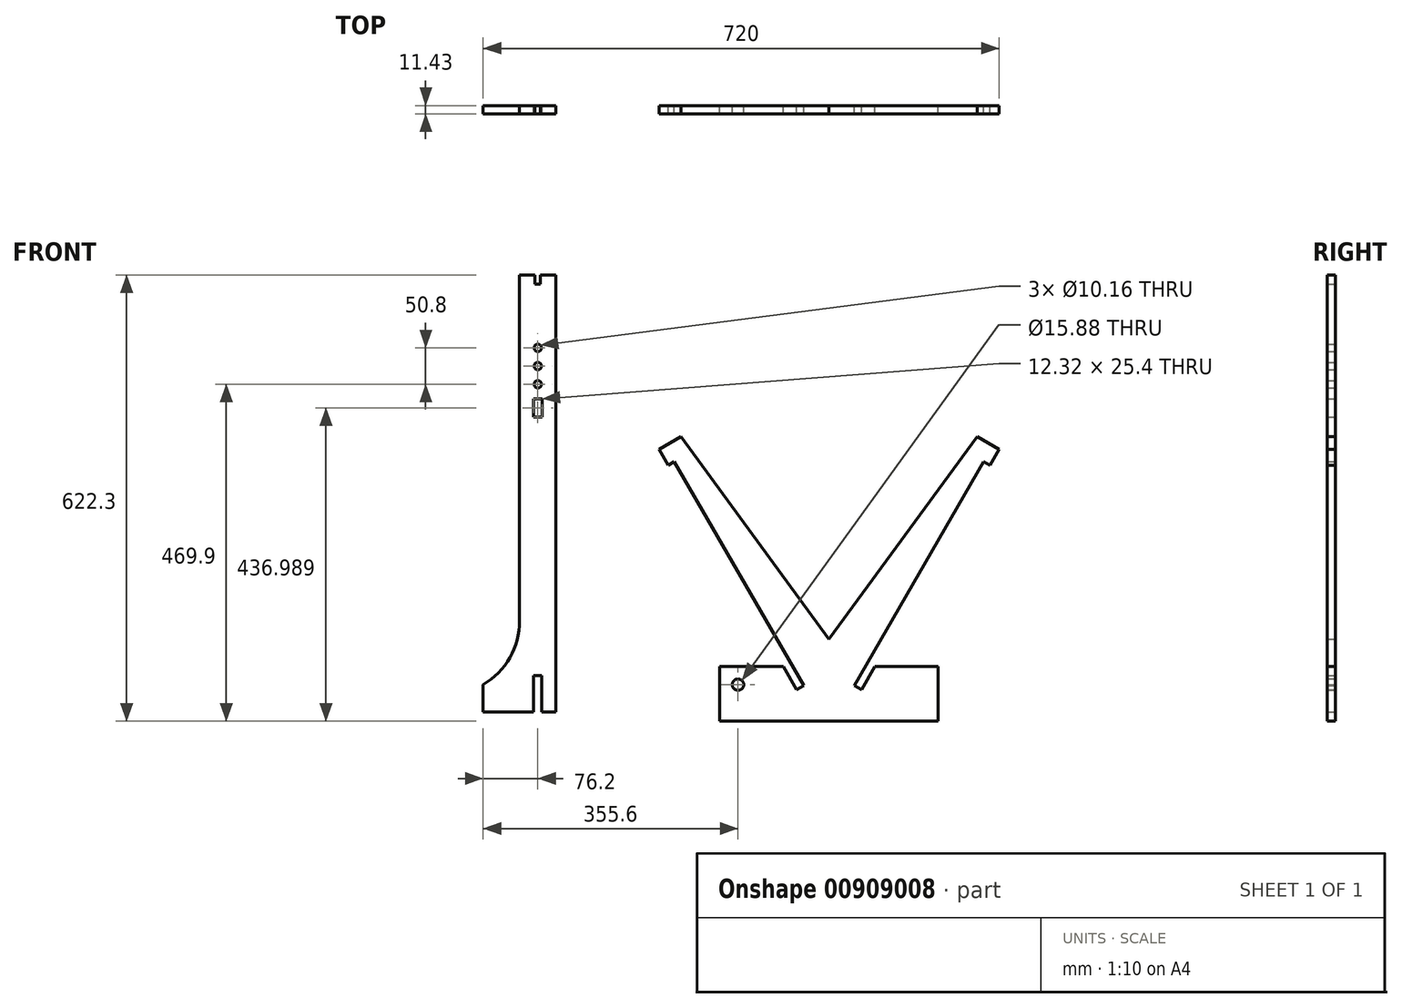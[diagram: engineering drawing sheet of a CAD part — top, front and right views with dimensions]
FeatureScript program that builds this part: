
annotation { "Feature Type Name" : "Feature", "Feature Type Description" : "" }
export const myFeature = defineFeature(function(context is Context, id is Id, definition is map)
    precondition{}
    {
        {
            var Q0;
            Q0=qCreatedBy(makeId("Front.planeOp"),FACE);
            var sketch = newSketch(context, id + "F0", { "sketchPlane" : qUnion([Q0])});
            skLineSegment(sketch, "E0.bottom", {"start": v(-25.4, 304.8) * mm, "end": v(25.4, 304.8) * mm});
            skLineSegment(sketch, "E0.top", {"start": v(-25.4, -304.8) * mm, "end": v(25.4, -304.8) * mm});
            skLineSegment(sketch, "E0.left", {"start": v(-25.4, 304.8) * mm, "end": v(-25.4, -304.8) * mm});
            skLineSegment(sketch, "E0.right", {"start": v(25.4, 304.8) * mm, "end": v(25.4, -304.8) * mm});
            skPoint(sketch, "E0.middle", {"position": v(0, 0) * mm});
            skLineSegment(sketch, "E1", {"start": v(-25.4, -304.8) * mm, "end": v(-76.2, -304.8) * mm});
            skLineSegment(sketch, "E2", {"start": v(-76.2, -304.8) * mm, "end": v(-76.2, -266.7) * mm});
            skArc(sketch, "E3", {"start": v(-76.2, -266.7) * mm, "mid": v(-39, -229) * mm, "end": v(-25.4, -177.8) * mm});
            skLineSegment(sketch, "E4", {"start": v(0, 0) * mm, "end": v(0, -304.8) * mm, "construction": true});
            skArc(sketch, "E5.MirrorCS", {"start": v(76.2, -266.7) * mm, "mid": v(39, -229) * mm, "end": v(25.4, -177.8) * mm});
            skLineSegment(sketch, "E6.MirrorCS", {"start": v(76.2, -304.8) * mm, "end": v(76.2, -266.7) * mm});
            skLineSegment(sketch, "E7.MirrorCS", {"start": v(25.4, -304.8) * mm, "end": v(76.2, -304.8) * mm});
            skLineSegment(sketch, "E8.bottom", {"start": v(-3.81, 304.8) * mm, "end": v(3.8, 304.8) * mm});
            skLineSegment(sketch, "E8.top", {"start": v(-3.81, 292.1) * mm, "end": v(3.8, 292.1) * mm});
            skLineSegment(sketch, "E8.left", {"start": v(-3.81, 304.8) * mm, "end": v(-3.81, 292.1) * mm});
            skLineSegment(sketch, "E8.right", {"start": v(3.8, 304.8) * mm, "end": v(3.8, 292.1) * mm});
            skPoint(sketch, "E8.middle", {"position": v(0, 298.45) * mm});
            skPoint(sketch, "E8.middle.positionSnap0", {"position": v(0, 304.8) * mm});
            skPoint(sketch, "E8.centerSnap0", {"position": v(0, 304.8) * mm});
            skLineSegment(sketch, "E9.bottom", {"start": v(5.72, -304.8) * mm, "end": v(-5.71, -304.8) * mm});
            skLineSegment(sketch, "E9.top", {"start": v(5.72, -254) * mm, "end": v(-5.71, -254) * mm});
            skLineSegment(sketch, "E9.left", {"start": v(5.72, -304.8) * mm, "end": v(5.72, -254) * mm});
            skLineSegment(sketch, "E9.right", {"start": v(-5.71, -304.8) * mm, "end": v(-5.71, -254) * mm});
            skPoint(sketch, "E9.middle", {"position": v(0, -279.4) * mm});
            skLineSegment(sketch, "E10.bottom", {"start": v(254, -317.5) * mm, "end": v(558.8, -317.5) * mm});
            skLineSegment(sketch, "E10.top", {"start": v(254, -241.3) * mm, "end": v(558.8, -241.3) * mm});
            skLineSegment(sketch, "E10.left", {"start": v(254, -317.5) * mm, "end": v(254, -241.3) * mm});
            skLineSegment(sketch, "E10.right", {"start": v(558.8, -317.5) * mm, "end": v(558.8, -241.3) * mm});
            skPoint(sketch, "E10.middle", {"position": v(406.4, -279.4) * mm});
            skLineSegment(sketch, "E11", {"start": v(355.6, -241.3) * mm, "end": v(370.9, -267.8) * mm});
            skLineSegment(sketch, "E12", {"start": v(370.9, -267.8) * mm, "end": v(361, -273.5) * mm});
            skLineSegment(sketch, "E13", {"start": v(361, -273.5) * mm, "end": v(342.4, -241.3) * mm});
            skLineSegment(sketch, "E14", {"start": v(406.4, -241.3) * mm, "end": v(406.4, -317.5) * mm, "construction": true});
            skLineSegment(sketch, "E15.MirrorCS", {"start": v(441.9, -267.8) * mm, "end": v(451.8, -273.5) * mm});
            skLineSegment(sketch, "E16.MirrorCS", {"start": v(451.8, -273.5) * mm, "end": v(470.4, -241.3) * mm});
            skLineSegment(sketch, "E17.MirrorCS", {"start": v(457.2, -241.3) * mm, "end": v(441.9, -267.8) * mm});
            skCircle(sketch, "E18", {"center": v(279.4, -266.7) * mm, "radius": 7.94 * mm});
            skPoint(sketch, "E18.centerSnap0", {"position": v(254, -279.4) * mm});
            skLineSegment(sketch, "E19", {"start": v(361, -273.5) * mm, "end": v(386.4, -317.5) * mm, "construction": true});
            skLineSegment(sketch, "E20", {"start": v(355.6, -241.3) * mm, "end": v(177.8, 66.66) * mm});
            skLineSegment(sketch, "E21", {"start": v(177.8, 66.66) * mm, "end": v(199.8, 79.36) * mm});
            skLineSegment(sketch, "E22", {"start": v(199.8, 79.36) * mm, "end": v(406.4, -203.2) * mm});
            skLineSegment(sketch, "E23.MirrorCS", {"start": v(613, 79.36) * mm, "end": v(406.4, -203.2) * mm});
            skLineSegment(sketch, "E24.MirrorCS", {"start": v(635, 66.66) * mm, "end": v(613, 79.36) * mm});
            skLineSegment(sketch, "E25.MirrorCS", {"start": v(457.2, -241.3) * mm, "end": v(635, 66.66) * mm});
            skCircle(sketch, "E26", {"center": v(0, 203.2) * mm, "radius": 5.08 * mm});
            skCircle(sketch, "E27.0.1.0", {"center": v(0, 177.8) * mm, "radius": 5.08 * mm});
            skCircle(sketch, "E27.0.2.0", {"center": v(0, 152.4) * mm, "radius": 5.08 * mm});
            skLineSegment(sketch, "E27.direction2", {"start": v(0, 203.2) * mm, "end": v(0, 177.8) * mm, "construction": true});
            skLineSegment(sketch, "E28", {"start": v(177.8, 66.66) * mm, "end": v(169, 61.58) * mm});
            skLineSegment(sketch, "E29", {"start": v(169, 61.58) * mm, "end": v(181.7, 39.58) * mm});
            skLineSegment(sketch, "E30", {"start": v(181.7, 39.58) * mm, "end": v(190.5, 44.66) * mm});
            skLineSegment(sketch, "E31.MirrorCS", {"start": v(631.1, 39.58) * mm, "end": v(622.3, 44.66) * mm});
            skLineSegment(sketch, "E32.MirrorCS", {"start": v(643.8, 61.58) * mm, "end": v(631.1, 39.58) * mm});
            skLineSegment(sketch, "E33.MirrorCS", {"start": v(635, 66.66) * mm, "end": v(643.8, 61.58) * mm});
            skLineSegment(sketch, "E34", {"start": v(365.95, -270.65) * mm, "end": v(185.55, 41.8) * mm, "construction": true});
            skLineSegment(sketch, "E35", {"start": v(86.79, -254) * mm, "end": v(86.79, 106.79) * mm, "construction": true});
            skLineSegment(sketch, "E36.top", {"start": v(-3.81, 311.15) * mm, "end": v(3.8, 311.15) * mm});
            skLineSegment(sketch, "E36.left", {"start": v(-3.81, 304.8) * mm, "end": v(-3.81, 311.15) * mm});
            skLineSegment(sketch, "E36.right", {"start": v(3.8, 304.8) * mm, "end": v(3.8, 311.15) * mm});
            skLineSegment(sketch, "E37.bottom", {"start": v(6.16, 106.79) * mm, "end": v(-6.16, 106.79) * mm});
            skLineSegment(sketch, "E37.top", {"start": v(6.16, 132.19) * mm, "end": v(-6.16, 132.19) * mm});
            skLineSegment(sketch, "E37.left", {"start": v(6.16, 106.79) * mm, "end": v(6.16, 132.19) * mm});
            skLineSegment(sketch, "E37.right", {"start": v(-6.16, 106.79) * mm, "end": v(-6.16, 132.19) * mm});
            skPoint(sketch, "E37.middle", {"position": v(0, 119.49) * mm});
            skSolve(sketch);
        }
        {
            var Q0;
            {var subQ2=sQuery(id+"F0.wireOp",EDGE,"E5.MirrorCS");Q0=makeQuery(id+"F0.imprint","IMPRINT",FACE,{"disambiguationData":[TD([[makeQuery(id+"F0.imprint","IMPRINT",EDGE,{"derivedFrom":subQ2}),1.0]])]});}
            var Q1;
            Q1=makeQuery(id+"F0.imprint","IMPRINT",FACE,{"disambiguationData":[TD([[makeQuery(id+"F0.imprint","IMPRINT",EDGE,{"derivedFrom":sQuery(id+"F0.wireOp",EDGE,"E8.top")}),-1.0]])]});
            var Q2;
            {var subQ0=sQuery(id+"F0.wireOp",EDGE,"E1");Q2=makeQuery(id+"F0.imprint","IMPRINT",FACE,{"disambiguationData":[TD([[makeQuery(id+"F0.imprint","IMPRINT",EDGE,{"derivedFrom":subQ0}),-1.0]])]});}
            var Q3;
            {var subQ0=sQuery(id+"F0.wireOp",EDGE,"E20");Q3=makeQuery(id+"F0.imprint","IMPRINT",FACE,{"disambiguationData":[TD([[makeQuery(id+"F0.imprint","IMPRINT",EDGE,{"derivedFrom":subQ0}),-1.0]])]});}
            var Q4;
            Q4=makeQuery(id+"F0.imprint","IMPRINT",FACE,{"disambiguationData":[TD([[makeQuery(id+"F0.imprint","IMPRINT",EDGE,{"derivedFrom":sQuery(id+"F0.wireOp",EDGE,"E10.bottom")}),1.0]])]});
            var Q5;
            {var subQ0=sQuery(id+"F0.wireOp",EDGE,"E28");Q5=makeQuery(id+"F0.imprint","IMPRINT",FACE,{"disambiguationData":[TD([[makeQuery(id+"F0.imprint","IMPRINT",EDGE,{"derivedFrom":subQ0}),1.0]])]});}
            var Q6;
            {var subQ2=sQuery(id+"F0.wireOp",EDGE,"E31.MirrorCS");Q6=makeQuery(id+"F0.imprint","IMPRINT",FACE,{"disambiguationData":[TD([[makeQuery(id+"F0.imprint","IMPRINT",EDGE,{"derivedFrom":subQ2}),-1.0]])]});}
            extrude(context, id + "F1", {"entities" : qUnion([Q0, Q1, Q2, Q3, Q4, Q5, Q6]), "depth" : 11.43 * mm, "offsetDistance" : 25.4 * mm});
        }
    });
